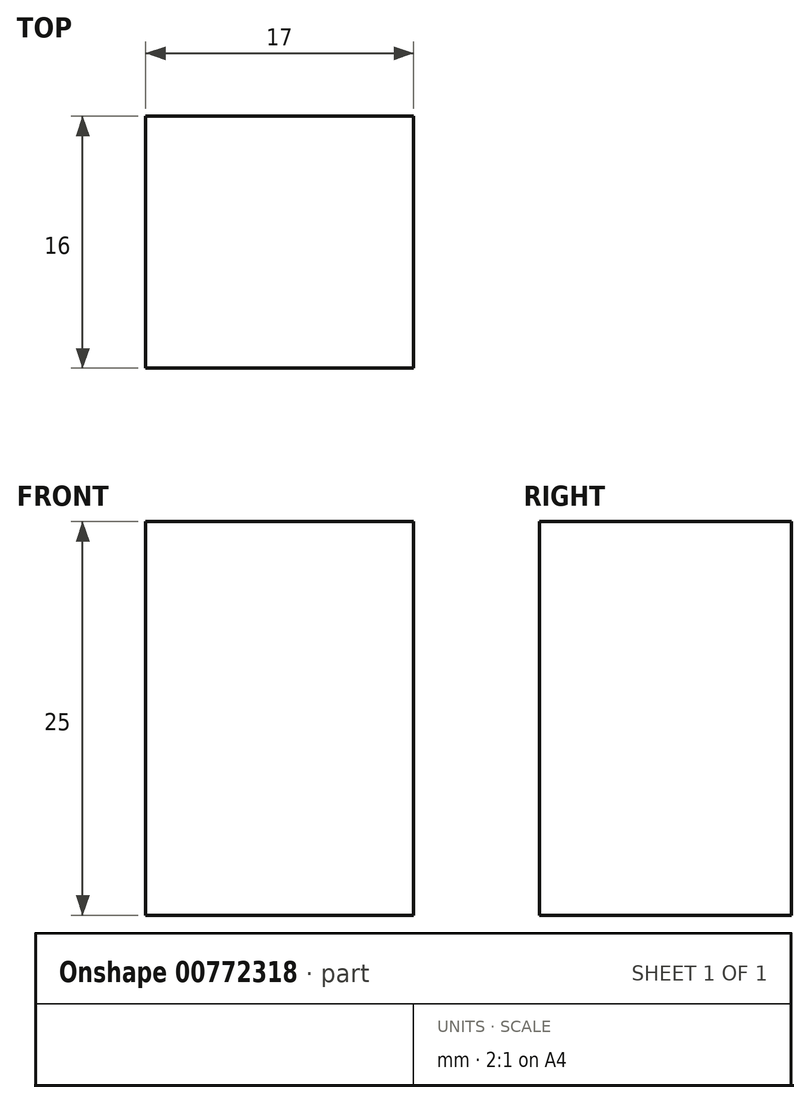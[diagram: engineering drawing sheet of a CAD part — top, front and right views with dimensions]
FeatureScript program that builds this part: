
annotation { "Feature Type Name" : "Feature", "Feature Type Description" : "" }
export const myFeature = defineFeature(function(context is Context, id is Id, definition is map)
    precondition{}
    {
        {
            var Q0;
            Q0=qCreatedBy(makeId("Front.planeOp"),FACE);
            var sketch = newSketch(context, id + "F0", { "sketchPlane" : qUnion([Q0])});
            skLineSegment(sketch, "E0.bottom", {"start": v(0, 25) * mm, "end": v(17, 25) * mm});
            skLineSegment(sketch, "E0.top", {"start": v(0, 0) * mm, "end": v(17, 0) * mm});
            skLineSegment(sketch, "E0.left", {"start": v(0, 25) * mm, "end": v(0, 0) * mm});
            skLineSegment(sketch, "E0.right", {"start": v(17, 25) * mm, "end": v(17, 0) * mm});
            skSolve(sketch);
        }
        {
            var Q0;
            Q0 = qSketchRegion(id + "F0", true);
            extrude(context, id + "F1", {"entities" : qUnion([Q0]), "depth" : 16 * mm, "offsetDistance" : 25 * mm});
        }
    });
